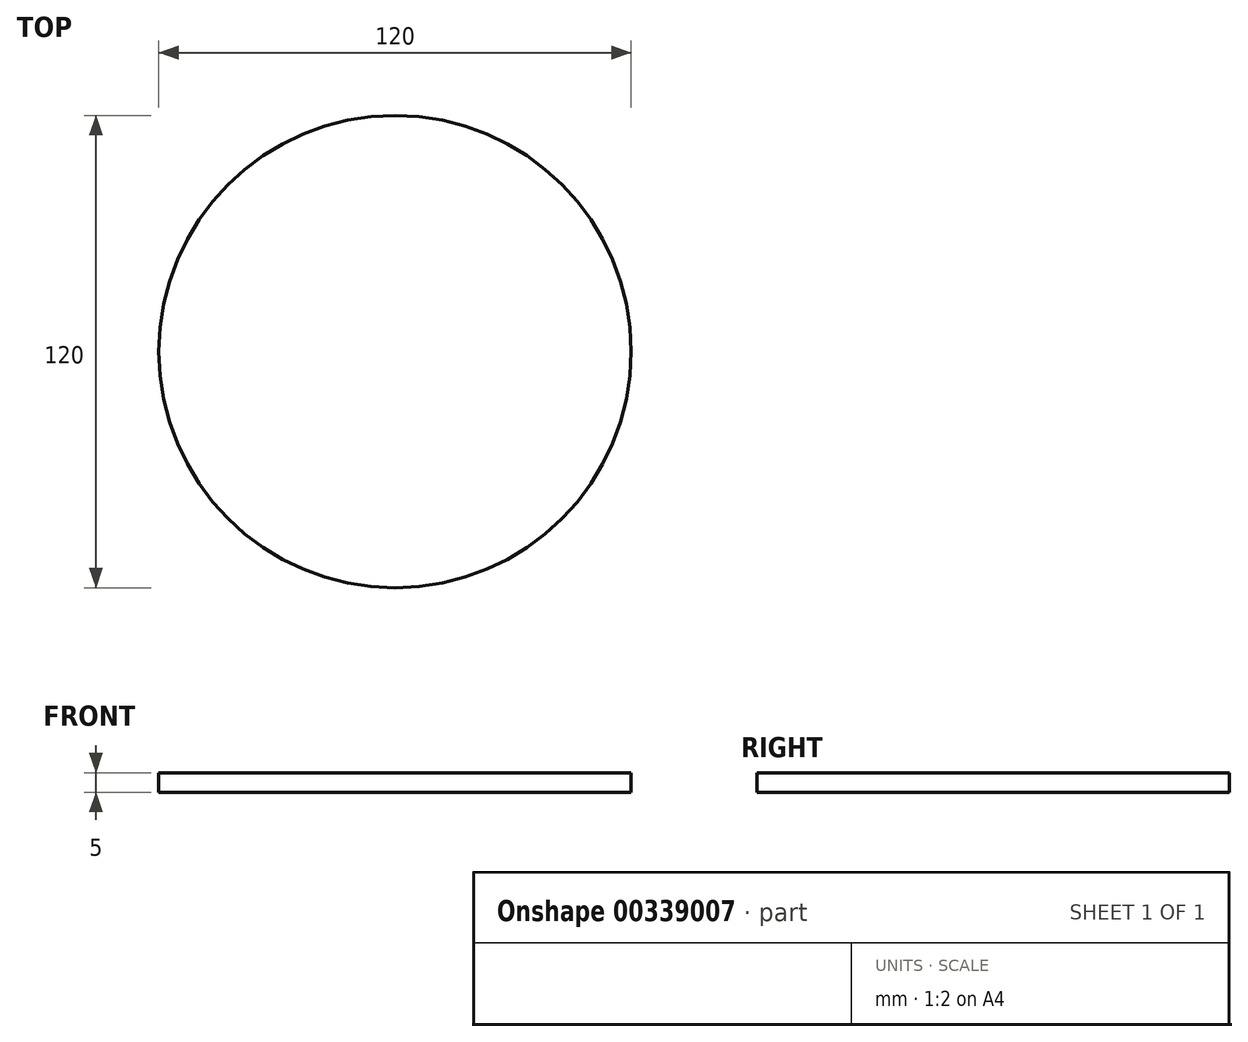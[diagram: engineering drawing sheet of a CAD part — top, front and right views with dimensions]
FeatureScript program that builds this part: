
annotation { "Feature Type Name" : "Feature", "Feature Type Description" : "" }
export const myFeature = defineFeature(function(context is Context, id is Id, definition is map)
    precondition{}
    {
        {
            var Q0;
            Q0=qCreatedBy(makeId("Top.planeOp"),FACE);
            var sketch = newSketch(context, id + "F0", { "sketchPlane" : qUnion([Q0])});
            skCircle(sketch, "E0", {"center": v(0, 0) * mm, "radius": 60 * mm});
            skSolve(sketch);
        }
        {
            var Q0;
            Q0 = qSketchRegion(id + "F0", true);
            extrude(context, id + "F1", {"entities" : qUnion([Q0]), "depth" : 5 * mm});
        }
    });
